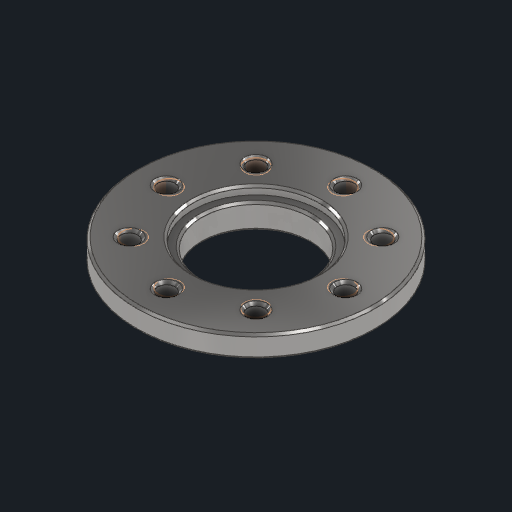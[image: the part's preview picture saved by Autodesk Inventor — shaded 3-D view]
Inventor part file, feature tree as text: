
AUTODESK INVENTOR PART (.ipt)
format: ipt  version: 2024 (Build 280153000, 153)  size: 269,312 bytes
history: native  units: mm
features: other x4, extrude x2, sketch x2, projected_geometry x2, chamfer x1
ambient origin geometry x8: Origin, YZ Plane, XZ Plane, XY Plane, X Axis, Y Axis, Z Axis, Center Point
bodies: Body1 (feature_tree), Body2 (feature_tree)
feature tree (11):
  other  "솔리드1"
  extrude  "돌출1"  Depth=16.5mm
  extrude  "돌출2"  Depth=80.0mm TaperAngle=360.0deg
  chamfer  "모따기1"  Distance=10.0mm
  sketch  "스케치1"
  projected_geometry  "투영된 루프1"
  sketch  "스케치2"
  projected_geometry  "투영된 루프2"
  other  "기준1"
  other  "복합1"
  other  "Srf1"
